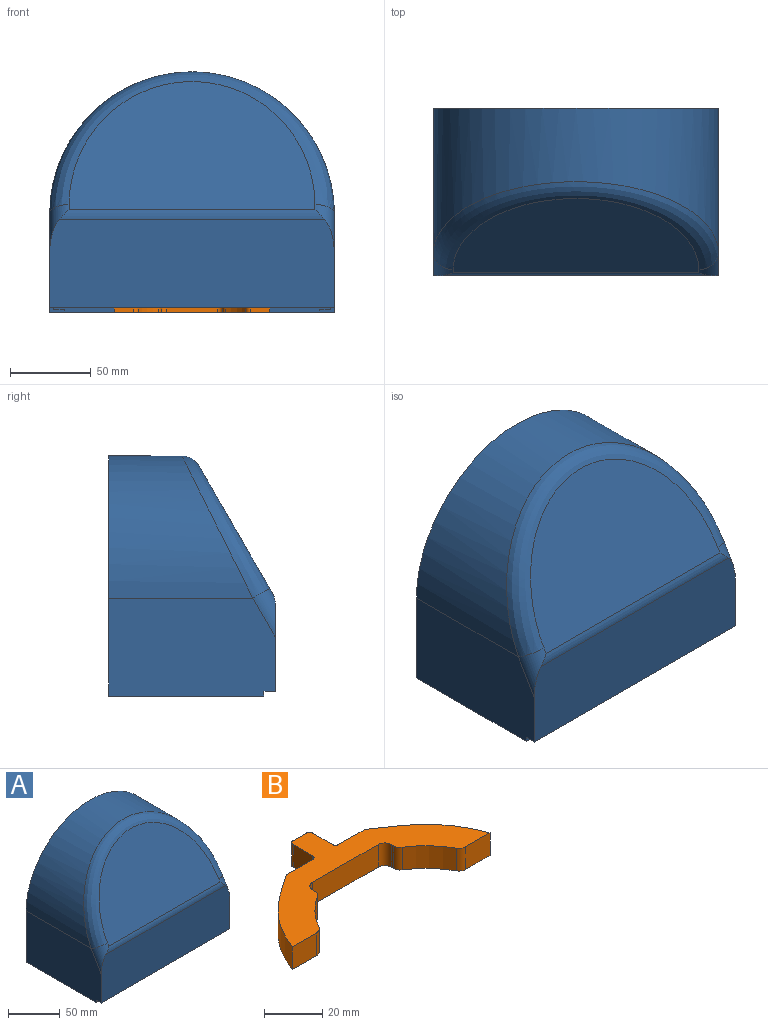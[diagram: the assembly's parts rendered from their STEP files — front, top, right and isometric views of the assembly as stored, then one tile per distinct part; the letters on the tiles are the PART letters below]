
ASSEMBLY  parts=2 mates=1
PART A: 29 faces, bbox 176.7x113.4x148.5 mm
  f0: plane 93.5x6.5mm, normal (0,0,1), area 607.8mm2, adj f1,f4,f10,f19
  f1: plane 93.5x1.5mm, normal (-1,0,0), area 140.3mm2, adj f0,f4,f5,f10
  f2: plane 103x60.5mm, normal (1,0,0), area 6044.2mm2, adj f3,f4,f5,f11,f12,f17,f27
  f3: plane 176x148.5mm, normal (0,1,0), area 10540.4mm2, adj f2,f5,f8,f12,f28
  f4: plane 9x3mm, normal (0,-1,0), area 17.2mm2, adj f0,f1,f2,f5,f19,f27
  f5: plane 176x96mm, normal (0,0,-1), area 2123mm2, adj f1,f2,f3,f4,f6,f8,f9,f10
  f6: plane 93.5x1.5mm, normal (1,0,0), area 140.3mm2, adj f5,f7,f9,f10
  f7: plane 93.5x6.5mm, normal (0,0,1), area 607.8mm2, adj f6,f9,f10,f20
  f8: plane 103x60.5mm, normal (-1,0,0), area 6044.2mm2, adj f3,f5,f9,f11,f12,f14,f27
  f9: plane 9x3mm, normal (0,-1,0), area 17.2mm2, adj f5,f6,f7,f8,f20,f27
  f10: plane 171x146mm, normal (0,-1,0), area 9537.1mm2, adj f0,f1,f5,f6,f7,f19,f20,f21
  f11: plane 176x54.28mm, normal (0,-1,0), area 9481.6mm2, adj f2,f8,f14,f15,f17,f27
  f12: cylinder r=88mm len=176mm, axis (0,-1,0), area 16922mm2, adj f2,f3,f8,f16
  f13: plane 152x79.22mm, normal (0,-0.87,0.5), area 11040.9mm2, adj f14,f15,f16,f17
  f14: cylinder r=12mm len=30mm, axis (0,-0.5,-0.87), area 266.2mm2, adj f8,f11,f13,f15,f16
  f15: cylinder r=12mm len=164mm, axis (1,0,0), area 993.6mm2, adj f11,f13,f14,f17
  f16: bspline ~176.67x103.29mm, area 4167.6mm2, adj f12,f13,f14,f17
  f17: cylinder r=12mm len=30mm, axis (0,-0.5,-0.87), area 266.2mm2, adj f2,f11,f13,f15,f16
  f18: plane 171x54.28mm, normal (0,1,0), area 9237.2mm2, adj f19,f20,f23,f24,f26,f27
  f19: plane 98x59mm, normal (-1,0,0), area 5663.6mm2, adj f0,f4,f10,f18,f21,f26,f27
  f20: plane 98x59mm, normal (1,0,0), area 5663.6mm2, adj f7,f9,f10,f18,f21,f23,f27
  f21: cylinder r=85.5mm len=171mm, axis (0,-1,0), area 15769.8mm2, adj f10,f19,f20,f25
  f22: plane 152x79.22mm, normal (0,0.87,-0.5), area 11040.9mm2, adj f23,f24,f25,f26
  f23: cylinder r=9.5mm len=24.42mm, axis (0,-0.5,-0.87), area 178.4mm2, adj f18,f20,f22,f24,f25
  f24: cylinder r=9.5mm len=161.5mm, axis (1,0,0), area 780.3mm2, adj f18,f22,f23,f26
  f25: bspline ~171.44x100.36mm, area 3249.6mm2, adj f21,f22,f23,f26
  f26: cylinder r=9.5mm len=24.42mm, axis (0,-0.5,-0.87), area 178.4mm2, adj f18,f19,f22,f24,f25
  f27: plane 176x7mm, normal (0,0,-1), area 462.5mm2, adj f2,f4,f8,f9,f11,f18,f19,f20
  f28: cylinder r=62.5mm len=125mm, axis (0,1,0), area 981.7mm2, adj f3,f10
PART B: 29 faces, bbox 95.9x44.5x9.5 mm
  f0: plane 9.53x9.5mm, normal (1,0,0), area 90.5mm2, adj f19,f20,f23,f24
  f1: plane 12.69x9.53mm, normal (0,1,0), area 120.8mm2, adj f2,f19,f20,f24
  f2: plane 10.05x9.53mm, normal (0.57,0.82,0), area 116.4mm2, adj f1,f3,f19,f20
  f3: cylinder r=3.43mm len=9.53mm, axis (0,0,1), area 0.4mm2, adj f2,f4,f19,f20
  f4: cylinder r=50.8mm len=24.78mm, axis (0,0,1), area 301mm2, adj f3,f5,f19,f20
  f5: plane 11.68x9.53mm, normal (0,-1,0), area 111.2mm2, adj f4,f6,f19,f20
  f6: cylinder r=3.43mm len=9.53mm, axis (0,0,1), area 34.7mm2, adj f5,f7,f19,f20
  f7: cylinder r=38.1mm len=13.52mm, axis (0,0,1), area 178.8mm2, adj f6,f19,f20,f27
  f8: plane 9.53x1.1mm, normal (-1,0,0), area 10.5mm2, adj f19,f20,f27,f28
  f9: plane 31.75x9.53mm, normal (0,-1,0), area 302.4mm2, adj f19,f20,f25,f28
  f10: plane 9.53x1.1mm, normal (1,0,0), area 10.5mm2, adj f19,f20,f25,f26
  f11: cylinder r=38.1mm len=13.52mm, axis (0,0,1), area 178.8mm2, adj f12,f19,f20,f26
  f12: cylinder r=3.43mm len=9.53mm, axis (0,0,1), area 34.7mm2, adj f11,f13,f19,f20
  f13: plane 11.68x9.53mm, normal (0,-1,0), area 111.2mm2, adj f12,f14,f19,f20
  f14: cylinder r=50.8mm len=24.78mm, axis (0,0,1), area 301mm2, adj f13,f15,f19,f20
  f15: plane 10.09x9.53mm, normal (-0.57,0.82,0), area 116.8mm2, adj f14,f16,f19,f20
  f16: plane 12.69x9.53mm, normal (0,1,0), area 120.8mm2, adj f15,f19,f20,f21
  f17: plane 9.53x9.5mm, normal (-1,0,0), area 90.5mm2, adj f19,f20,f21,f22
  f18: plane 9.53x6.32mm, normal (0,1,0), area 60.2mm2, adj f19,f20,f22,f23
  f19: plane 95.86x44.45mm, normal (0,0,-1), area 1330.1mm2, adj f0,f1,f2,f3,f4,f5,f6,f7
  f20: plane 95.86x44.45mm, normal (0,0,1), area 1330.1mm2, adj f0,f1,f2,f3,f4,f5,f6,f7
  f21: cylinder r=1.6mm len=9.53mm, axis (0,0,1), area 23.9mm2, adj f16,f17,f19,f20
  f22: cylinder r=1.6mm len=9.53mm, axis (0,0,-1), area 23.9mm2, adj f17,f18,f19,f20
  f23: cylinder r=1.6mm len=9.53mm, axis (0,0,1), area 23.9mm2, adj f0,f18,f19,f20
  f24: cylinder r=1.6mm len=9.53mm, axis (0,0,-1), area 23.9mm2, adj f0,f1,f19,f20
  f25: cylinder r=3.17mm len=9.53mm, axis (0,0,-1), area 47.5mm2, adj f9,f10,f19,f20
  f26: cylinder r=3.17mm len=9.53mm, axis (0,0,1), area 30.3mm2, adj f10,f11,f19,f20
  f27: cylinder r=3.17mm len=9.53mm, axis (0,0,1), area 30.3mm2, adj f7,f8,f19,f20
  f28: cylinder r=3.17mm len=9.53mm, axis (0,0,1), area 47.5mm2, adj f8,f9,f19,f20
PLACE A at identity fixed
PLACE B t=(0,-27.68,19.85)mm
MATE fastened B.f19 <-> A.f5  axis (0,0,-1) through (0,8.7,1.5)mm
